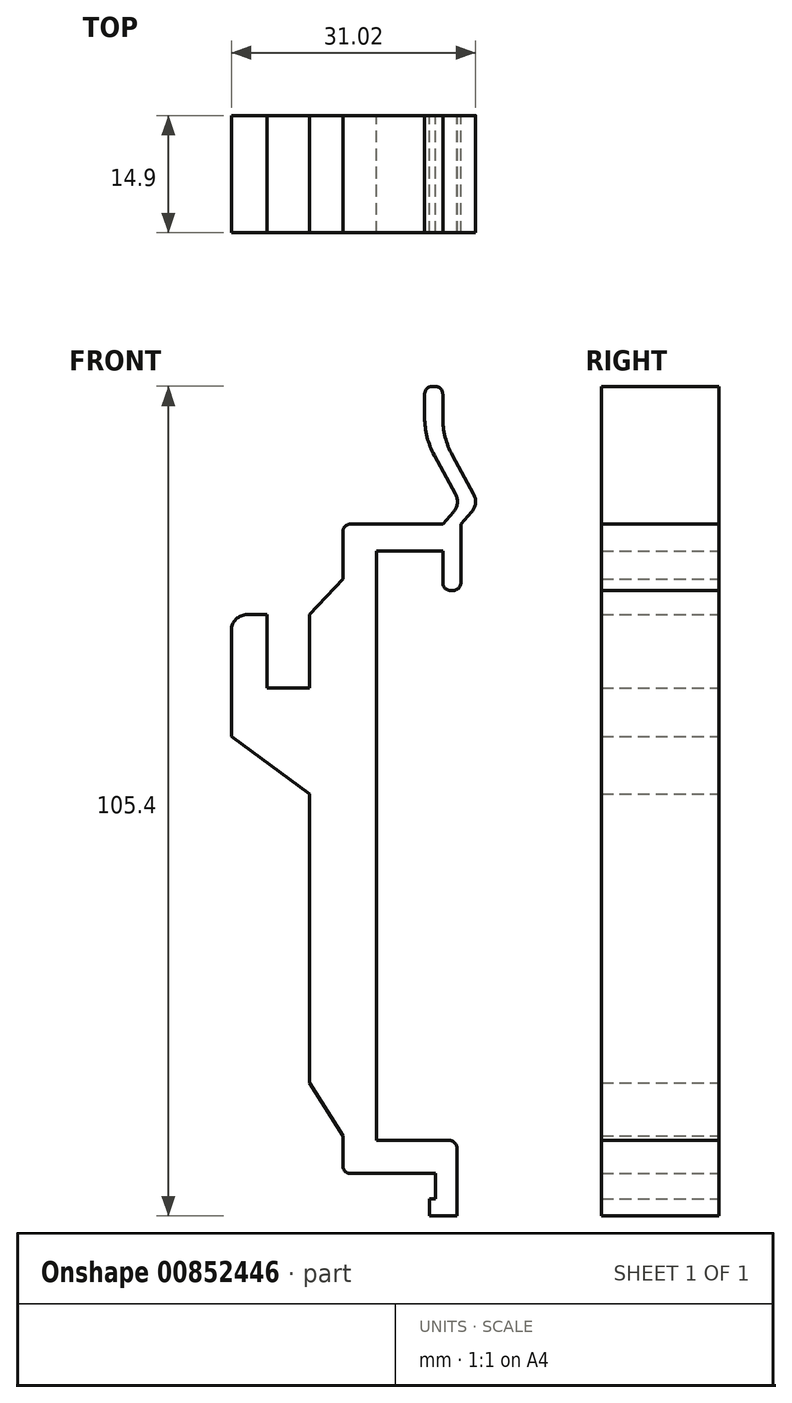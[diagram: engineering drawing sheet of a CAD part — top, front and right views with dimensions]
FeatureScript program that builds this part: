
annotation { "Feature Type Name" : "Feature", "Feature Type Description" : "" }
export const myFeature = defineFeature(function(context is Context, id is Id, definition is map)
    precondition{}
    {
        {
            var Q0;
            Q0=qCreatedBy(makeId("Front.planeOp"),FACE);
            var sketch = newSketch(context, id + "F0", { "sketchPlane" : qUnion([Q0])});
            skLineSegment(sketch, "E0", {"start": v(-4.3, -36.83) * mm, "end": v(-8.5, -30.1) * mm});
            skLineSegment(sketch, "E1", {"start": v(-8.5, -30.1) * mm, "end": v(-8.5, 6.6) * mm});
            skLineSegment(sketch, "E2", {"start": v(-8.5, 6.6) * mm, "end": v(-18.45, 13.87) * mm});
            skLineSegment(sketch, "E3", {"start": v(-18.45, 13.87) * mm, "end": v(-18.45, 27.37) * mm});
            skLineSegment(sketch, "E4", {"start": v(-16.45, 29.37) * mm, "end": v(-13.95, 29.37) * mm});
            skLineSegment(sketch, "E5", {"start": v(-13.95, 29.38) * mm, "end": v(-13.95, 20.08) * mm});
            skLineSegment(sketch, "E6", {"start": v(-13.95, 20.07) * mm, "end": v(-8.5, 20.08) * mm});
            skLineSegment(sketch, "E7", {"start": v(-8.5, 20.08) * mm, "end": v(-8.5, 29.38) * mm});
            skLineSegment(sketch, "E8", {"start": v(-8.5, 29.37) * mm, "end": v(-4.3, 33.87) * mm});
            skLineSegment(sketch, "E9", {"start": v(-4.3, 33.87) * mm, "end": v(-4.3, 39.88) * mm});
            skLineSegment(sketch, "E10", {"start": v(-3.3, 40.88) * mm, "end": v(8.4, 40.88) * mm});
            skLineSegment(sketch, "E11", {"start": v(10.7, 40.88) * mm, "end": v(10.7, 33.43) * mm});
            skLineSegment(sketch, "E12", {"start": v(9.7, 32.43) * mm, "end": v(9.4, 32.43) * mm});
            skLineSegment(sketch, "E13", {"start": v(8.4, 33.43) * mm, "end": v(8.4, 37.43) * mm});
            skLineSegment(sketch, "E14", {"start": v(8.4, 37.43) * mm, "end": v(0, 37.42) * mm});
            skLineSegment(sketch, "E15", {"start": v(0, 37.42) * mm, "end": v(0, -37.42) * mm});
            skLineSegment(sketch, "E16", {"start": v(0, -37.42) * mm, "end": v(9.2, -37.42) * mm});
            skLineSegment(sketch, "E17", {"start": v(10.2, -38.42) * mm, "end": v(10.2, -47.02) * mm});
            skLineSegment(sketch, "E18", {"start": v(10.2, -47.02) * mm, "end": v(6.7, -47.02) * mm});
            skLineSegment(sketch, "E19", {"start": v(6.7, -47.02) * mm, "end": v(6.7, -44.82) * mm});
            skLineSegment(sketch, "E20", {"start": v(6.7, -44.82) * mm, "end": v(7.45, -44.82) * mm});
            skLineSegment(sketch, "E21", {"start": v(7.45, -44.82) * mm, "end": v(7.45, -41.62) * mm});
            skLineSegment(sketch, "E22", {"start": v(7.45, -41.62) * mm, "end": v(-3.3, -41.62) * mm});
            skLineSegment(sketch, "E23", {"start": v(-4.3, -40.62) * mm, "end": v(-4.3, -36.83) * mm});
            skLineSegment(sketch, "E24", {"start": v(8.4, 57.38) * mm, "end": v(8.4, 54.41) * mm});
            skLineSegment(sketch, "E25", {"start": v(9.63, 49.61) * mm, "end": v(12.32, 44.69) * mm});
            skLineSegment(sketch, "E26", {"start": v(12.06, 42.4) * mm, "end": v(10.7, 40.87) * mm});
            skLineSegment(sketch, "E27", {"start": v(7.4, 58.38) * mm, "end": v(7.1, 58.38) * mm});
            skLineSegment(sketch, "E28", {"start": v(6.1, 57.38) * mm, "end": v(6.1, 54.41) * mm});
            skLineSegment(sketch, "E29", {"start": v(7.33, 49.61) * mm, "end": v(10.02, 44.69) * mm});
            skLineSegment(sketch, "E30", {"start": v(9.76, 42.4) * mm, "end": v(8.4, 40.88) * mm});
            skPoint(sketch, "E31.visualSharp", {"position": v(6.1, 51.86) * mm});
            skArc(sketch, "E31.filletArc", {"start": v(6.1, 54.41) * mm, "mid": v(6.41, 51.94) * mm, "end": v(7.33, 49.61) * mm});
            skPoint(sketch, "E32.visualSharp", {"position": v(8.4, 51.86) * mm});
            skArc(sketch, "E32.filletArc", {"start": v(8.4, 54.41) * mm, "mid": v(8.71, 51.94) * mm, "end": v(9.63, 49.61) * mm});
            skPoint(sketch, "E33.visualSharp", {"position": v(10.7, 43.45) * mm});
            skArc(sketch, "E33.filletArc", {"start": v(9.76, 42.4) * mm, "mid": v(10.25, 43.5) * mm, "end": v(10.02, 44.69) * mm});
            skPoint(sketch, "E34.visualSharp", {"position": v(13, 43.45) * mm});
            skArc(sketch, "E34.filletArc", {"start": v(12.06, 42.4) * mm, "mid": v(12.55, 43.5) * mm, "end": v(12.32, 44.69) * mm});
            skPoint(sketch, "E35.visualSharp", {"position": v(8.4, 58.38) * mm});
            skArc(sketch, "E35.filletArc", {"start": v(8.4, 57.38) * mm, "mid": v(8.1, 58.08) * mm, "end": v(7.4, 58.38) * mm});
            skPoint(sketch, "E36.visualSharp", {"position": v(6.1, 58.38) * mm});
            skArc(sketch, "E36.filletArc", {"start": v(7.1, 58.38) * mm, "mid": v(6.4, 58.08) * mm, "end": v(6.1, 57.38) * mm});
            skPoint(sketch, "E37.visualSharp", {"position": v(10.7, 32.43) * mm});
            skArc(sketch, "E37.filletArc", {"start": v(9.7, 32.43) * mm, "mid": v(10.4, 32.72) * mm, "end": v(10.7, 33.43) * mm});
            skPoint(sketch, "E38.visualSharp", {"position": v(8.4, 32.43) * mm});
            skArc(sketch, "E38.filletArc", {"start": v(8.4, 33.43) * mm, "mid": v(8.7, 32.72) * mm, "end": v(9.4, 32.43) * mm});
            skPoint(sketch, "E39.visualSharp", {"position": v(-4.3, 40.87) * mm});
            skArc(sketch, "E39.filletArc", {"start": v(-3.3, 40.88) * mm, "mid": v(-4, 40.58) * mm, "end": v(-4.3, 39.88) * mm});
            skPoint(sketch, "E40.visualSharp", {"position": v(-18.45, 29.37) * mm});
            skArc(sketch, "E40.filletArc", {"start": v(-16.45, 29.38) * mm, "mid": v(-17.86, 28.79) * mm, "end": v(-18.45, 27.37) * mm});
            skPoint(sketch, "E41.visualSharp", {"position": v(-4.3, -41.62) * mm});
            skArc(sketch, "E41.filletArc", {"start": v(-4.3, -40.62) * mm, "mid": v(-4, -41.33) * mm, "end": v(-3.3, -41.62) * mm});
            skPoint(sketch, "E42.visualSharp", {"position": v(10.2, -37.42) * mm});
            skArc(sketch, "E42.filletArc", {"start": v(10.2, -38.42) * mm, "mid": v(9.9, -37.72) * mm, "end": v(9.2, -37.42) * mm});
            skSolve(sketch);
        }
        {
            var Q0;
            Q0=qSketchRegion(id+"F0",true);
            extrude(context, id + "F1", {"entities" : qUnion([Q0]), "depth" : 14.9 * mm, "symmetric" : true});
        }
    });
